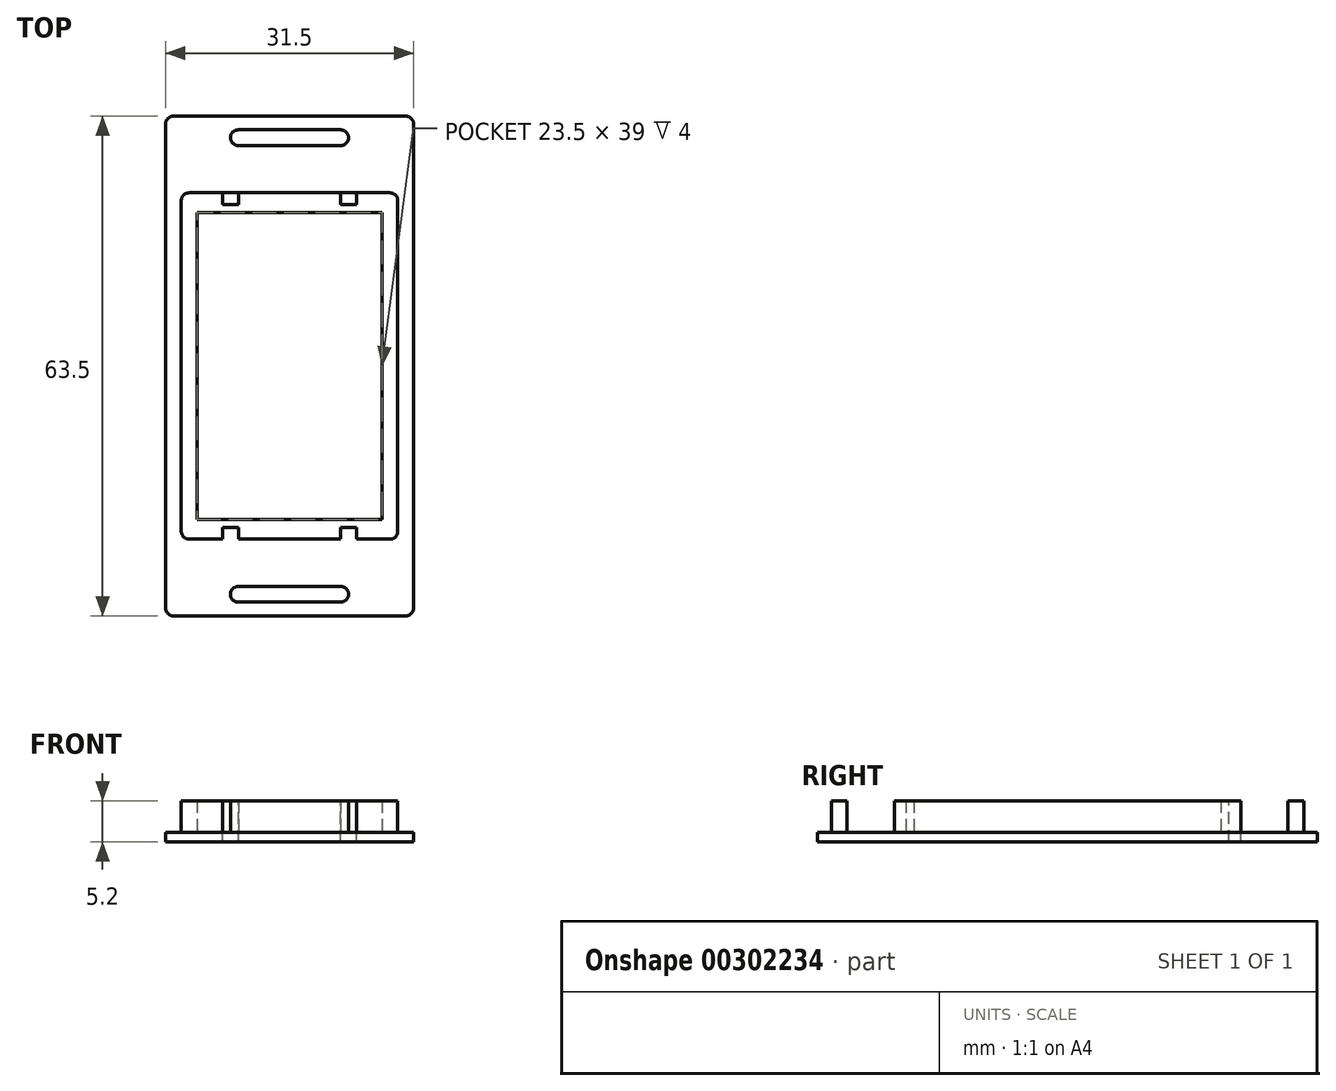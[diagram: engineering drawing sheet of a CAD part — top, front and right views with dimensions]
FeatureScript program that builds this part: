
annotation { "Feature Type Name" : "Feature", "Feature Type Description" : "" }
export const myFeature = defineFeature(function(context is Context, id is Id, definition is map)
    precondition{}
    {
        {
            var Q0;
            Q0=qCreatedBy(makeId("Top.planeOp"),FACE);
            var sketch = newSketch(context, id + "F0", { "sketchPlane" : qUnion([Q0])});
            skLineSegment(sketch, "E0.bottom", {"start": v(13.75, -30) * mm, "end": v(-13.75, -30) * mm});
            skLineSegment(sketch, "E0.top", {"start": v(13.75, 30) * mm, "end": v(-13.75, 30) * mm});
            skLineSegment(sketch, "E0.left", {"start": v(13.75, -30) * mm, "end": v(13.75, 30) * mm});
            skLineSegment(sketch, "E0.right", {"start": v(-13.75, -30) * mm, "end": v(-13.75, 30) * mm});
            skPoint(sketch, "E0.middle", {"position": v(0, 0) * mm});
            skLineSegment(sketch, "E1.bottom", {"start": v(15.75, -31.75) * mm, "end": v(-15.75, -31.75) * mm});
            skLineSegment(sketch, "E1.top", {"start": v(15.75, 31.75) * mm, "end": v(-15.75, 31.75) * mm});
            skLineSegment(sketch, "E1.left", {"start": v(15.75, -31.75) * mm, "end": v(15.75, 31.75) * mm});
            skLineSegment(sketch, "E1.right", {"start": v(-15.75, -31.75) * mm, "end": v(-15.75, 31.75) * mm});
            skLineSegment(sketch, "E2.bottom", {"start": v(11.75, -28) * mm, "end": v(-11.75, -28) * mm});
            skLineSegment(sketch, "E2.top", {"start": v(11.75, 28) * mm, "end": v(-11.75, 28) * mm});
            skLineSegment(sketch, "E2.left", {"start": v(11.75, -28) * mm, "end": v(11.75, 28) * mm});
            skLineSegment(sketch, "E2.right", {"start": v(-11.75, -28) * mm, "end": v(-11.75, 28) * mm});
            skLineSegment(sketch, "E3", {"start": v(-13.75, -22) * mm, "end": v(13.75, -22) * mm});
            skLineSegment(sketch, "E4", {"start": v(-13.75, 22) * mm, "end": v(13.75, 22) * mm});
            skLineSegment(sketch, "E5", {"start": v(-11.75, -19.5) * mm, "end": v(11.75, -19.5) * mm});
            skLineSegment(sketch, "E6", {"start": v(-11.75, 19.5) * mm, "end": v(11.75, 19.5) * mm});
            skLineSegment(sketch, "E7", {"start": v(0, 31.75) * mm, "end": v(0, -31.75) * mm, "construction": true});
            skLineSegment(sketch, "E8", {"start": v(-7.5, 30) * mm, "end": v(-7.5, 28) * mm});
            skLineSegment(sketch, "E9", {"start": v(7.5, 30) * mm, "end": v(7.5, 28) * mm});
            skLineSegment(sketch, "E10", {"start": v(-7.5, -28) * mm, "end": v(-7.5, -30) * mm});
            skPoint(sketch, "E10.endSnap0", {"position": v(0, -30) * mm});
            skLineSegment(sketch, "E11", {"start": v(7.5, -28) * mm, "end": v(7.5, -30) * mm});
            skLineSegment(sketch, "E12.bottom", {"start": v(-6.5, 22) * mm, "end": v(-8.5, 22) * mm});
            skLineSegment(sketch, "E12.top", {"start": v(-6.5, 20.5) * mm, "end": v(-8.5, 20.5) * mm});
            skLineSegment(sketch, "E12.left", {"start": v(-6.5, 22) * mm, "end": v(-6.5, 20.5) * mm});
            skLineSegment(sketch, "E12.right", {"start": v(-8.5, 22) * mm, "end": v(-8.5, 20.5) * mm});
            skLineSegment(sketch, "E13.bottom", {"start": v(6.5, 22) * mm, "end": v(8.5, 22) * mm});
            skLineSegment(sketch, "E13.top", {"start": v(6.5, 20.5) * mm, "end": v(8.5, 20.5) * mm});
            skLineSegment(sketch, "E13.left", {"start": v(6.5, 22) * mm, "end": v(6.5, 20.5) * mm});
            skLineSegment(sketch, "E13.right", {"start": v(8.5, 22) * mm, "end": v(8.5, 20.5) * mm});
            skLineSegment(sketch, "E14", {"start": v(-11.75, 0) * mm, "end": v(11.75, 0) * mm, "construction": true});
            skLineSegment(sketch, "E15.MirrorCS", {"start": v(-8.5, -22) * mm, "end": v(-8.5, -20.5) * mm});
            skLineSegment(sketch, "E16.MirrorCS", {"start": v(-6.5, -20.5) * mm, "end": v(-8.5, -20.5) * mm});
            skLineSegment(sketch, "E17.MirrorCS", {"start": v(-6.5, -22) * mm, "end": v(-6.5, -20.5) * mm});
            skLineSegment(sketch, "E18.MirrorCS", {"start": v(6.5, -22) * mm, "end": v(6.5, -20.5) * mm});
            skLineSegment(sketch, "E19.MirrorCS", {"start": v(6.5, -20.5) * mm, "end": v(8.5, -20.5) * mm});
            skLineSegment(sketch, "E20.MirrorCS", {"start": v(8.5, -22) * mm, "end": v(8.5, -20.5) * mm});
            skSolve(sketch);
        }
        {
            var Q0;
            {var subQ0=sQuery(id+"F0.wireOp",EDGE,"E3");var subQ1=sQuery(id+"F0.wireOp",EDGE,"E0.right");var subQ2=makeQuery(id+"F0.imprint","INTERSECT",VERTEX,{"derivedFrom":[subQ1,subQ0]});Q0=makeQuery(id+"F0.imprint","IMPRINT",FACE,{"disambiguationData":[TD([[makeQuery(id+"F0.imprint","IMPRINT",EDGE,{"disambiguationData":[TD([[subQ2,-1.0]])],"derivedFrom":subQ1}),-1.0]])]});}
            var Q1;
            {var subQ0=sQuery(id+"F0.wireOp",EDGE,"E3");var subQ1=sQuery(id+"F0.wireOp",EDGE,"E0.left");var subQ2=makeQuery(id+"F0.imprint","INTERSECT",VERTEX,{"derivedFrom":[subQ1,subQ0]});Q1=makeQuery(id+"F0.imprint","IMPRINT",FACE,{"disambiguationData":[TD([[makeQuery(id+"F0.imprint","IMPRINT",EDGE,{"disambiguationData":[TD([[subQ2,-1.0]])],"derivedFrom":subQ1}),1.0]])]});}
            var Q2;
            {var subQ0=sQuery(id+"F0.wireOp",EDGE,"E3");var subQ1=sQuery(id+"F0.wireOp",EDGE,"E2.left");var subQ2=makeQuery(id+"F0.imprint","INTERSECT",VERTEX,{"derivedFrom":[subQ1,subQ0]});Q2=makeQuery(id+"F0.imprint","IMPRINT",FACE,{"disambiguationData":[TD([[makeQuery(id+"F0.imprint","IMPRINT",EDGE,{"disambiguationData":[TD([[subQ2,-1.0]])],"derivedFrom":subQ1}),1.0]])]});}
            var Q3;
            {var subQ0=sQuery(id+"F0.wireOp",EDGE,"E2.bottom");Q3=makeQuery(id+"F0.imprint","IMPRINT",FACE,{"disambiguationData":[TD([[makeQuery(id+"F0.imprint","IMPRINT",EDGE,{"derivedFrom":subQ0}),-1.0]])]});}
            var Q4;
            {var subQ6=sQuery(id+"F0.wireOp",EDGE,"E0.bottom");Q4=makeQuery(id+"F0.imprint","IMPRINT",FACE,{"disambiguationData":[TD([[makeQuery(id+"F0.imprint","IMPRINT",EDGE,{"derivedFrom":subQ6}),1.0]])]});}
            var Q5;
            {var subQ2=sQuery(id+"F0.wireOp",EDGE,"E0.bottom");Q5=makeQuery(id+"F0.imprint","IMPRINT",FACE,{"disambiguationData":[TD([[makeQuery(id+"F0.imprint","IMPRINT",EDGE,{"derivedFrom":subQ2}),-1.0]])]});}
            var Q6;
            {var subQ0=sQuery(id+"F0.wireOp",EDGE,"E2.top");Q6=makeQuery(id+"F0.imprint","IMPRINT",FACE,{"disambiguationData":[TD([[makeQuery(id+"F0.imprint","IMPRINT",EDGE,{"derivedFrom":subQ0}),1.0]])]});}
            var Q7;
            {var subQ2=sQuery(id+"F0.wireOp",EDGE,"E0.top");Q7=makeQuery(id+"F0.imprint","IMPRINT",FACE,{"disambiguationData":[TD([[makeQuery(id+"F0.imprint","IMPRINT",EDGE,{"derivedFrom":subQ2}),1.0]])]});}
            var Q8;
            {var subQ0=sQuery(id+"F0.wireOp",EDGE,"E5");Q8=makeQuery(id+"F0.imprint","IMPRINT",FACE,{"disambiguationData":[TD([[makeQuery(id+"F0.imprint","IMPRINT",EDGE,{"derivedFrom":subQ0}),1.0]])]});}
            var Q9;
            {var subQ0=sQuery(id+"F0.wireOp",EDGE,"E6");Q9=makeQuery(id+"F0.imprint","IMPRINT",FACE,{"disambiguationData":[TD([[makeQuery(id+"F0.imprint","IMPRINT",EDGE,{"derivedFrom":subQ0}),1.0]])]});}
            var Q10;
            {var subQ5=sQuery(id+"F0.wireOp",EDGE,"E8");Q10=makeQuery(id+"F0.imprint","IMPRINT",FACE,{"disambiguationData":[TD([[makeQuery(id+"F0.imprint","IMPRINT",EDGE,{"derivedFrom":subQ5}),-1.0]])]});}
            var Q11;
            {var subQ7=sQuery(id+"F0.wireOp",EDGE,"E9");Q11=makeQuery(id+"F0.imprint","IMPRINT",FACE,{"disambiguationData":[TD([[makeQuery(id+"F0.imprint","IMPRINT",EDGE,{"derivedFrom":subQ7}),1.0]])]});}
            var Q12;
            {var subQ3=sQuery(id+"F0.wireOp",EDGE,"E10");Q12=makeQuery(id+"F0.imprint","IMPRINT",FACE,{"disambiguationData":[TD([[makeQuery(id+"F0.imprint","IMPRINT",EDGE,{"derivedFrom":subQ3}),-1.0]])]});}
            var Q13;
            {var subQ8=sQuery(id+"F0.wireOp",EDGE,"E11");Q13=makeQuery(id+"F0.imprint","IMPRINT",FACE,{"disambiguationData":[TD([[makeQuery(id+"F0.imprint","IMPRINT",EDGE,{"derivedFrom":subQ8}),1.0]])]});}
            var Q14;
            Q14=makeQuery(id+"F0.imprint","IMPRINT",FACE,{"disambiguationData":[TD([[makeQuery(id+"F0.imprint","IMPRINT",EDGE,{"derivedFrom":sQuery(id+"F0.wireOp",EDGE,"E12.bottom")}),1.0]])]});
            var Q15;
            Q15=makeQuery(id+"F0.imprint","IMPRINT",FACE,{"disambiguationData":[TD([[makeQuery(id+"F0.imprint","IMPRINT",EDGE,{"derivedFrom":sQuery(id+"F0.wireOp",EDGE,"E13.bottom")}),-1.0]])]});
            var Q16;
            {var subQ0=sQuery(id+"F0.wireOp",EDGE,"E15.MirrorCS");Q16=makeQuery(id+"F0.imprint","IMPRINT",FACE,{"disambiguationData":[TD([[makeQuery(id+"F0.imprint","IMPRINT",EDGE,{"derivedFrom":subQ0}),-1.0]])]});}
            var Q17;
            {var subQ0=sQuery(id+"F0.wireOp",EDGE,"E18.MirrorCS");Q17=makeQuery(id+"F0.imprint","IMPRINT",FACE,{"disambiguationData":[TD([[makeQuery(id+"F0.imprint","IMPRINT",EDGE,{"derivedFrom":subQ0}),-1.0]])]});}
            extrude(context, id + "F1", {"entities" : qUnion([Q0, Q1, Q2, Q3, Q4, Q5, Q6, Q7, Q8, Q9, Q10, Q11, Q12, Q13, Q14, Q15, Q16, Q17]), "oppositeDirection" : true, "depth" : 1.2 * mm});
        }
        {
            var Q0;
            {var subQ5=sQuery(id+"F0.wireOp",EDGE,"E3");var subQ7=sQuery(id+"F0.wireOp",EDGE,"E0.right");var subQ8=makeQuery(id+"F0.imprint","INTERSECT",VERTEX,{"derivedFrom":[subQ7,subQ5]});Q0=makeQuery(id+"F0.imprint","IMPRINT",FACE,{"disambiguationData":[TD([[makeQuery(id+"F0.imprint","IMPRINT",EDGE,{"disambiguationData":[TD([[subQ8,-1.0]])],"derivedFrom":subQ7}),-1.0]])]});}
            var Q1;
            {var subQ0=sQuery(id+"F0.wireOp",EDGE,"E6");Q1=makeQuery(id+"F0.imprint","IMPRINT",FACE,{"disambiguationData":[TD([[makeQuery(id+"F0.imprint","IMPRINT",EDGE,{"derivedFrom":subQ0}),1.0]])]});}
            var Q2;
            {var subQ5=sQuery(id+"F0.wireOp",EDGE,"E3");var subQ7=sQuery(id+"F0.wireOp",EDGE,"E0.left");var subQ8=makeQuery(id+"F0.imprint","INTERSECT",VERTEX,{"derivedFrom":[subQ7,subQ5]});Q2=makeQuery(id+"F0.imprint","IMPRINT",FACE,{"disambiguationData":[TD([[makeQuery(id+"F0.imprint","IMPRINT",EDGE,{"disambiguationData":[TD([[subQ8,-1.0]])],"derivedFrom":subQ7}),1.0]])]});}
            var Q3;
            {var subQ0=sQuery(id+"F0.wireOp",EDGE,"E5");Q3=makeQuery(id+"F0.imprint","IMPRINT",FACE,{"disambiguationData":[TD([[makeQuery(id+"F0.imprint","IMPRINT",EDGE,{"derivedFrom":subQ0}),-1.0]])]});}
            var Q4;
            {var subQ0=sQuery(id+"F0.wireOp",EDGE,"E8");Q4=makeQuery(id+"F0.imprint","IMPRINT",FACE,{"disambiguationData":[TD([[makeQuery(id+"F0.imprint","IMPRINT",EDGE,{"derivedFrom":subQ0}),1.0]])]});}
            var Q5;
            {var subQ0=sQuery(id+"F0.wireOp",EDGE,"E10");Q5=makeQuery(id+"F0.imprint","IMPRINT",FACE,{"disambiguationData":[TD([[makeQuery(id+"F0.imprint","IMPRINT",EDGE,{"derivedFrom":subQ0}),1.0]])]});}
            extrude(context, id + "F2", {"entities" : qUnion([Q0, Q1, Q2, Q3, Q4, Q5]), "operationType" : NewBodyOperationType.ADD, "depth" : 4 * mm});
        }
        {
            var Q0;
            Q0=makeQuery(id+"F2.opExtrude","SWEPT_EDGE",EDGE,{"disambiguationData":[OSD([sQuery(id+"F0.wireOp",EDGE,"E0.right"),sQuery(id+"F0.wireOp",EDGE,"E4")])]});
            var Q1;
            Q1=makeQuery(id+"F2.opExtrude","SWEPT_EDGE",EDGE,{"disambiguationData":[OSD([sQuery(id+"F0.wireOp",EDGE,"E0.left"),sQuery(id+"F0.wireOp",EDGE,"E4")])]});
            var Q2;
            Q2=makeQuery(id+"F2.opExtrude","SWEPT_EDGE",EDGE,{"disambiguationData":[OSD([sQuery(id+"F0.wireOp",EDGE,"E0.left"),sQuery(id+"F0.wireOp",EDGE,"E3")])]});
            var Q3;
            Q3=makeQuery(id+"F2.opExtrude","SWEPT_EDGE",EDGE,{"disambiguationData":[OSD([sQuery(id+"F0.wireOp",EDGE,"E0.right"),sQuery(id+"F0.wireOp",EDGE,"E3")])]});
            var Q4;
            Q4=makeQuery(id+"F1.opExtrude","SWEPT_EDGE",EDGE,{"disambiguationData":[OSD([sQuery(id+"F0.wireOp",EDGE,"E1.bottom"),sQuery(id+"F0.wireOp",EDGE,"E1.right")])]});
            var Q5;
            Q5=makeQuery(id+"F1.opExtrude","SWEPT_EDGE",EDGE,{"disambiguationData":[OSD([sQuery(id+"F0.wireOp",EDGE,"E1.bottom"),sQuery(id+"F0.wireOp",EDGE,"E1.left")])]});
            var Q6;
            Q6=makeQuery(id+"F1.opExtrude","SWEPT_EDGE",EDGE,{"disambiguationData":[OSD([sQuery(id+"F0.wireOp",EDGE,"E1.top"),sQuery(id+"F0.wireOp",EDGE,"E1.right")])]});
            var Q7;
            Q7=makeQuery(id+"F1.opExtrude","SWEPT_EDGE",EDGE,{"disambiguationData":[OSD([sQuery(id+"F0.wireOp",EDGE,"E1.top"),sQuery(id+"F0.wireOp",EDGE,"E1.left")])]});
            var Q8;
            Q8=makeQuery(id+"F2.opExtrude","SWEPT_EDGE",EDGE,{"disambiguationData":[OSD([sQuery(id+"F0.wireOp",EDGE,"E0.bottom"),sQuery(id+"F0.wireOp",EDGE,"E10")])]});
            var Q9;
            Q9=makeQuery(id+"F2.opExtrude","SWEPT_EDGE",EDGE,{"disambiguationData":[OSD([sQuery(id+"F0.wireOp",EDGE,"E0.bottom"),sQuery(id+"F0.wireOp",EDGE,"E11")])]});
            var Q10;
            Q10=makeQuery(id+"F2.opExtrude","SWEPT_EDGE",EDGE,{"disambiguationData":[OSD([sQuery(id+"F0.wireOp",EDGE,"E2.bottom"),sQuery(id+"F0.wireOp",EDGE,"E11")])]});
            var Q11;
            Q11=makeQuery(id+"F2.opExtrude","SWEPT_EDGE",EDGE,{"disambiguationData":[OSD([sQuery(id+"F0.wireOp",EDGE,"E2.bottom"),sQuery(id+"F0.wireOp",EDGE,"E10")])]});
            var Q12;
            Q12=makeQuery(id+"F2.opExtrude","SWEPT_EDGE",EDGE,{"disambiguationData":[OSD([sQuery(id+"F0.wireOp",EDGE,"E2.top"),sQuery(id+"F0.wireOp",EDGE,"E8")])]});
            var Q13;
            Q13=makeQuery(id+"F2.opExtrude","SWEPT_EDGE",EDGE,{"disambiguationData":[OSD([sQuery(id+"F0.wireOp",EDGE,"E2.top"),sQuery(id+"F0.wireOp",EDGE,"E9")])]});
            var Q14;
            Q14=makeQuery(id+"F2.opExtrude","SWEPT_EDGE",EDGE,{"disambiguationData":[OSD([sQuery(id+"F0.wireOp",EDGE,"E0.top"),sQuery(id+"F0.wireOp",EDGE,"E9")])]});
            var Q15;
            Q15=makeQuery(id+"F2.opExtrude","SWEPT_EDGE",EDGE,{"disambiguationData":[OSD([sQuery(id+"F0.wireOp",EDGE,"E0.top"),sQuery(id+"F0.wireOp",EDGE,"E8")])]});
            fillet(context, id + "F3", {"entities" : qUnion([Q0, Q1, Q2, Q3, Q4, Q5, Q6, Q7, Q8, Q9, Q10, Q11, Q12, Q13, Q14, Q15]), "radius" : 1 * mm, "tangentPropagation" : true, "allowEdgeOverflow" : false});
        }
    });
